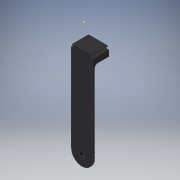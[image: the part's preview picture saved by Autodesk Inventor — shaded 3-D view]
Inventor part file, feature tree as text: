
AUTODESK INVENTOR PART (.ipt)
format: ipt  version: 2018 (Build 220112000, 112)  size: 215,040 bytes
history: native  units: mm
features: sketch x5, extrude x3, projected_geometry x3, hole x1, fillet x1
ambient origin geometry x8: Origin, YZ Plane, XZ Plane, XY Plane, X Axis, Y Axis, Z Axis, Center Point
bodies: Solid1 (feature_tree)
feature tree (13):
  extrude  "Extrusion1"  Depth=5.0mm TaperAngle=0.0deg
  extrude  "Extrusion2"  Depth=37.0mm TaperAngle=0.0deg
  sketch  "Sketch3"  dims[d8=26.0mm d9=15.5mm d10=0.0mm]
  extrude  "Extrusion3"  Depth=15.5mm TaperAngle=0.0deg
  hole  "Hole1"  [1 undecoded]
  fillet  "Fillet1"  [1 undecoded]
  sketch  "Sketch1"  dims[d1=0.3mm d3=5.0mm d4=0.0mm]
  sketch  "Sketch2"  dims[d5=16.0mm d6=37.0mm d7=0.0mm]
  projected_geometry  "Projected Loop1"
  sketch  "Sketch4"  dims[d11=10.0mm]
  projected_geometry  "Projected Loop2"
  sketch  "Sketch5"  dims[d12=7.0mm d13=6.0mm d14=11.0mm d15=8.0mm d16=90.0deg d17=8.0mm d18=20.594885mm d19=8.0mm]
  projected_geometry  "Projected Loop3"
note: 2 required parameter values undecoded (feature->parameter linkage not recoverable at this tier; creation-order binding heuristic only, values carry confidence <= 0.55)
